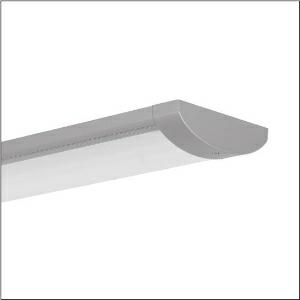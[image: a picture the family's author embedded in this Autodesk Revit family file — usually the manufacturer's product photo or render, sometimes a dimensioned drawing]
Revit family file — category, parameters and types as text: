
# Revit family: tv_20_5xa86172n0a
name_source: partatom
category: Lighting Fixtures
units: mm (PartAtom-declared; Revit-internal decimal feet)

## family parameters
Cut with Voids When Loaded = No
Host = Face
Light Source = No
Part Type = Normal
Room Calculation Point = No
Round Connector Dimension = Use Diameter
Shared = No

## types (1)
- TV 20 (1 x LED 4000K / CRI = 80 (unbekannt), 2130 lm, 4000K)
    Apparent Load = 21 VA
    CIE Flux Codes = 48 78 95 99 100
    Color Rendering = 80
    Color Temperature = 4000K
    Default Elevation = 1800 mm
    Description = TV 20, vandal-proof luminaire, primary light control with specular reflector, of aluminium, matt, primary optical cover: enclosure, of PC, frosted, light emission: direct distribution, primary light characteristic: symmetric, installation type: surface-mounted, LED rated luminous flux: 2.130 lm, light colour: 840, colour temperature: 4000K, control gear: ECG, mains connection: 230V, AC, 50Hz, rated input power: 21W, luminaire housing, of aluminium, coated, Siteco® metallic grey (DB 702S), length: 705 mm, width: 260 mm, height: 70mm, protection rating (complete): IP65, insulation class (complete): insulation class I (protective earthing), certification: CE, protection symbol: F, impact resistance: 2x IK10, standard: EN 60598, packaging unit: 1 piece
    Height = 70 mm
    Lamp = 1 x LED 4000K / CRI >= 80 (unbekannt)
    Lamp Light Flux = 2130 lm
    Lamp count = 1
    Length = 705 mm
    Luminous efficacy = 101 lm/W
    Manufacturer = Siteco
    ModVariant = No
    Model = 5XA86172N0A
    Mounting Place = Ceiling
    Mounting Type = Surface mounted
    Number of Poles = 1
    OnlyDefault = Yes
    Power Factor = 1
    Product Name = TV 20
    Product group = vandal-proof luminaire
    ProductGroupID = 307
    Protection Class = Protection class I
    Protection Degree = IP 65
    RLX_Detail_Level = 1
    RlxData = <blob elided: 34157 chars, md5=7fa677f6>
    Socket = socket
    Standby Power = 0 W
    System Light Flux = 2130 lm
    System Power = 21 W
    Type Comments = Product without accessories
    Type Image = l_1004809.jpg
    URL = http://relux.com
    VarID = ---
    Voltage = 0 V
    Weight = 0.00 kg
    Width = 260 mm

## geometry (parser evidence)
native form markers: Blend x4, Sweep x9
no freeform markers — native parametric forms only
